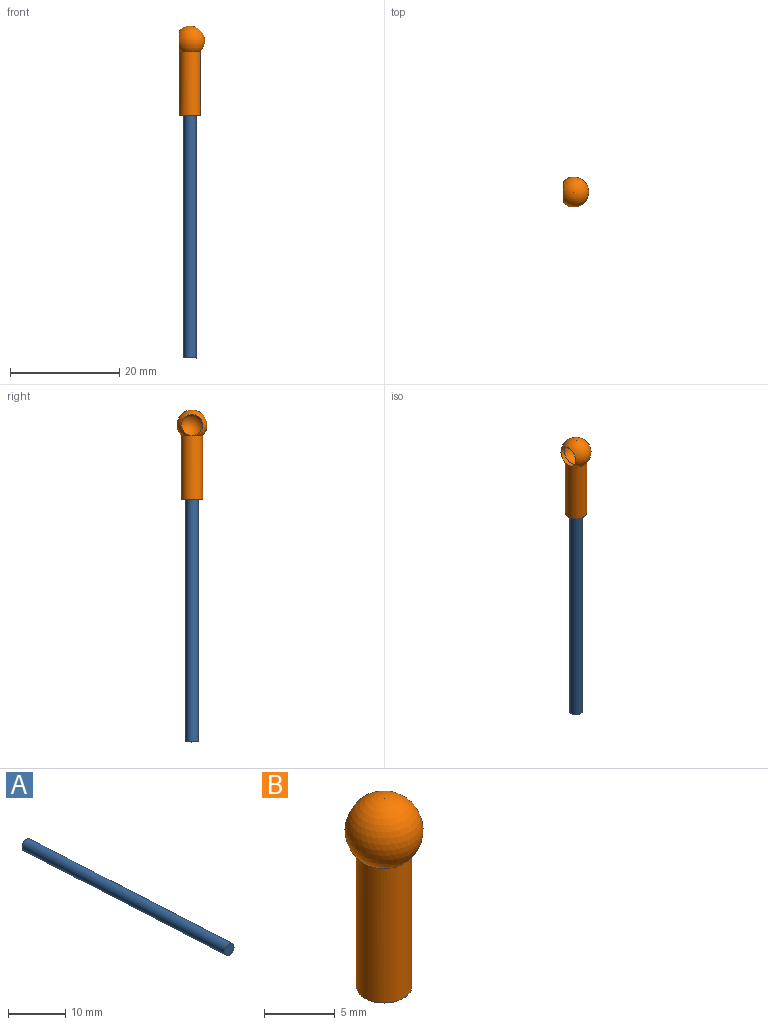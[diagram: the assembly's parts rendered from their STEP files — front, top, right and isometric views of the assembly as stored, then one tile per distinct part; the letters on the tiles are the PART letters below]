
ASSEMBLY  parts=2 mates=1
PART A: 3 faces, bbox 2.3x50.1x4.9 mm
  f0: plane 2.3x2.3mm, normal (0,-1,0.05), area 4.2mm2, adj f1
  f1: cylinder r=1.15mm len=50.05mm, axis (0,1,-0.05), area 361.3mm2, adj f0,f2
  f2: plane 2.3x2.3mm, normal (0,1,-0.05), area 4.2mm2, adj f1
PART B: 7 faces, bbox 5.5x5.5x16.3 mm
  f0: cylinder r=1.94mm len=3.88mm, axis (0,-1,0), area 9.9mm2, adj f1,f6
  f1: sphere r=2.25mm, area 47.9mm2, adj f0
  f2: plane 3.9x3.9mm, normal (0,0,-1), area 7.8mm2, adj f3,f4
  f3: cylinder r=1.95mm len=11.61mm, axis (0,0,1), area 142.3mm2, adj f2,f6
  f4: cylinder r=1.15mm len=11.05mm, axis (0,0,1), area 79.9mm2, adj f2,f5
  f5: sphere r=2.75mm, area 4.4mm2, adj f4
  f6: sphere r=2.75mm, area 67.2mm2, adj f0,f3
PLACE A rot(axis=(0.59,0.59,0.56),121.7deg) t=(27.7,-20.25,-49.53)mm
PLACE B rot(axis=(0,0,1),90deg) t=(34.93,10,0.45)mm
MATE fastened A.f1 <-> B.f3  axis (0,0,1) through (34.93,10,5.98)mm
